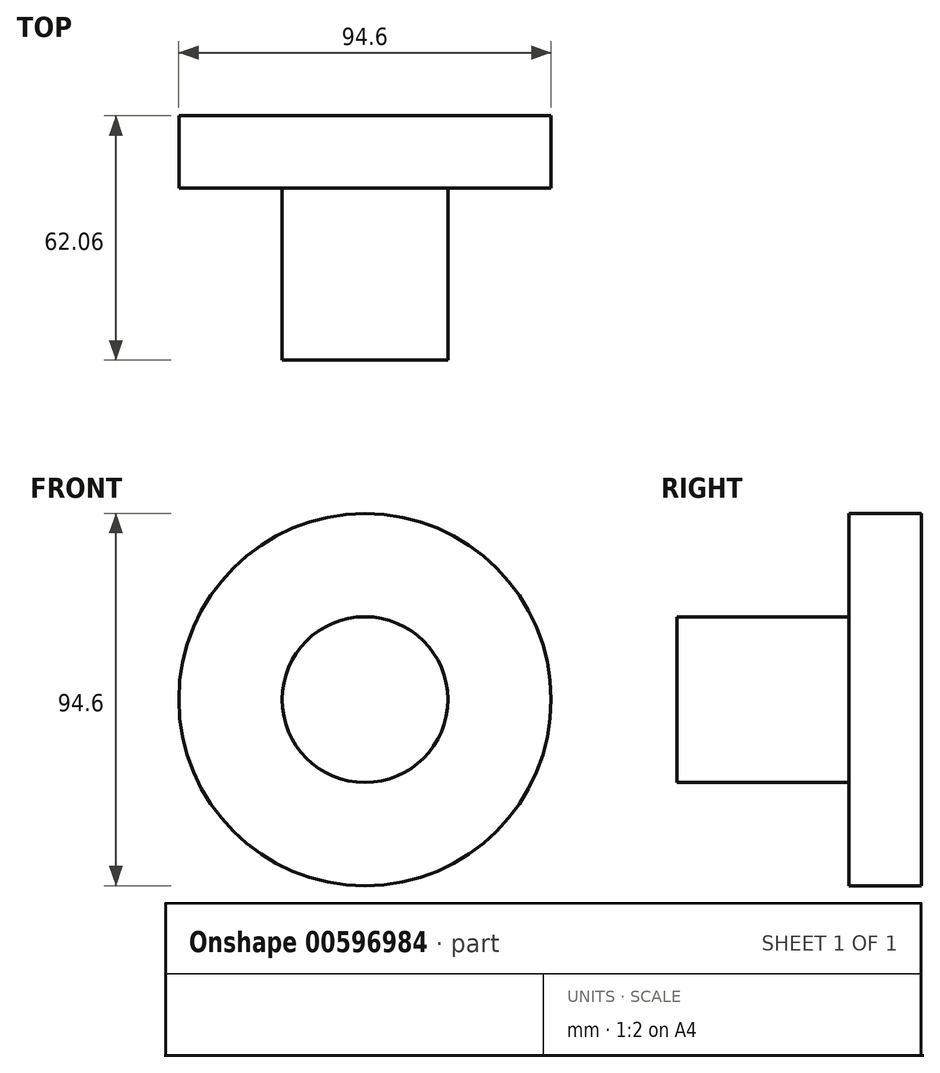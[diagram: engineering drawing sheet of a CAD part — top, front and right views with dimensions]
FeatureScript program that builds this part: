
annotation { "Feature Type Name" : "Feature", "Feature Type Description" : "" }
export const myFeature = defineFeature(function(context is Context, id is Id, definition is map)
    precondition{}
    {
        {
            var Q0;
            Q0=qCreatedBy(makeId("Top.planeOp"),FACE);
            var sketch = newSketch(context, id + "F0", { "sketchPlane" : qUnion([Q0])});
            skLineSegment(sketch, "E0", {"start": v(0, 0) * mm, "end": v(21.05, 0) * mm});
            skLineSegment(sketch, "E1", {"start": v(21.05, 0) * mm, "end": v(21.05, 43.65) * mm});
            skLineSegment(sketch, "E2", {"start": v(21.05, 43.65) * mm, "end": v(47.3, 43.65) * mm});
            skLineSegment(sketch, "E3", {"start": v(47.3, 43.65) * mm, "end": v(47.3, 62.06) * mm});
            skLineSegment(sketch, "E4", {"start": v(47.3, 62.06) * mm, "end": v(0, 62.06) * mm});
            skLineSegment(sketch, "E5", {"start": v(0, 62.06) * mm, "end": v(0, 0) * mm});
            skSolve(sketch);
        }
        {
            var Q0;
            Q0 = qSketchRegion(id + "F0", true);
            var Q1;
            Q1=sQuery(id+"F0.wireOp",EDGE,"E5");
            revolve(context, id + "F1", {"entities" : qUnion([Q0]), "axis" : qUnion([Q1]), "revolveType" : RevolveType.FULL});
        }
    });
